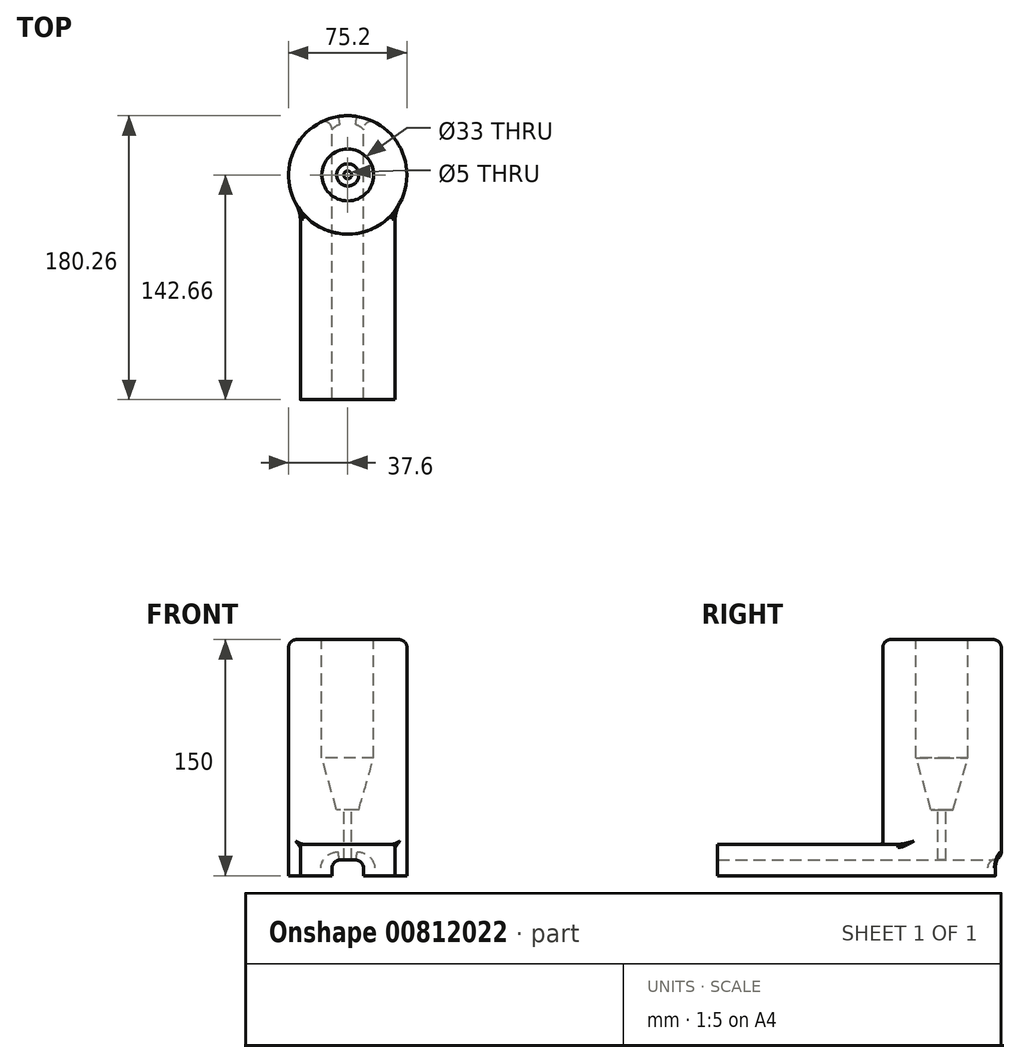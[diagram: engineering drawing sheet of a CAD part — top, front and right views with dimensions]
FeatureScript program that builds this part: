
annotation { "Feature Type Name" : "Feature", "Feature Type Description" : "" }
export const myFeature = defineFeature(function(context is Context, id is Id, definition is map)
    precondition{}
    {
        {
            var Q0;
            Q0=qCreatedBy(makeId("Front.planeOp"),FACE);
            var sketch = newSketch(context, id + "F0", { "sketchPlane" : qUnion([Q0])});
            skLineSegment(sketch, "E0.bottom", {"start": v(0, 0) * mm, "end": v(60, 0) * mm});
            skLineSegment(sketch, "E0.top", {"start": v(0, 20) * mm, "end": v(60, 20) * mm});
            skLineSegment(sketch, "E0.left", {"start": v(0, 0) * mm, "end": v(0, 20) * mm});
            skLineSegment(sketch, "E0.right", {"start": v(60, 0) * mm, "end": v(60, 20) * mm});
            skLineSegment(sketch, "E1.bottom", {"start": v(20, 0) * mm, "end": v(40, 0) * mm});
            skLineSegment(sketch, "E1.top", {"start": v(20, 10) * mm, "end": v(40, 10) * mm});
            skLineSegment(sketch, "E1.left", {"start": v(20, 0) * mm, "end": v(20, 10) * mm});
            skLineSegment(sketch, "E1.right", {"start": v(40, 0) * mm, "end": v(40, 10) * mm});
            skSolve(sketch);
        }
        {
            var Q0;
            Q0=makeQuery(id+"F0.imprint","IMPRINT",FACE,{"disambiguationData":[TD([[makeQuery(id+"F0.imprint","IMPRINT",EDGE,{"derivedFrom":sQuery(id+"F0.wireOp",EDGE,"E0.top")}),-1.0]])]});
            extrude(context, id + "F1", {"entities" : qUnion([Q0]), "depth" : 120 * mm, "offsetDistance" : 25 * mm});
        }
        {
            var Q0;
            Q0=qCreatedBy(makeId("Top.planeOp"),FACE);
            var sketch = newSketch(context, id + "F2", { "sketchPlane" : qUnion([Q0])});
            skPoint(sketch, "E2.0", {"position": v(60, 0) * mm});
            skCircle(sketch, "E3", {"center": v(30, 22.66) * mm, "radius": 37.6 * mm});
            skPoint(sketch, "E3.first.point", {"position": v(0, 0) * mm});
            skPoint(sketch, "E3.third.point", {"position": v(-4.6, 37.36) * mm});
            skSolve(sketch);
        }
        {
            var Q0;
            Q0=qSketchRegion(id+"F2",true);
            extrude(context, id + "F3", {"entities" : qUnion([Q0]), "operationType" : NewBodyOperationType.ADD, "depth" : 150 * mm, "offsetDistance" : 25 * mm});
        }
        {
            var Q0;
            Q0=makeQuery(id+"F0.imprint","IMPRINT",FACE,{"disambiguationData":[TD([[makeQuery(id+"F0.imprint","IMPRINT",EDGE,{"derivedFrom":sQuery(id+"F0.wireOp",EDGE,"E1.top")}),-1.0]])]});
            extrude(context, id + "F4", {"entities" : qUnion([Q0]), "operationType" : NewBodyOperationType.REMOVE, "endBound" : BoundingType.UP_TO_NEXT, "oppositeDirection" : true, "depth" : 25 * mm, "offsetDistance" : 25 * mm, "hasSecondDirection" : true, "secondDirectionOppositeDirection" : false, "secondDirectionDepth" : 25 * mm});
        }
        {
            var Q0;
            Q0=makeQuery(id+"F1.opExtrude","CAP_EDGE",EDGE,{"disambiguationData":[OSD([sQuery(id+"F0.wireOp",EDGE,"E0.right")])],"isStart":true});
            var Q1;
            Q1=makeQuery(id+"F1.opExtrude","CAP_EDGE",EDGE,{"disambiguationData":[OSD([sQuery(id+"F0.wireOp",EDGE,"E0.left")])],"isStart":true});
            fillet(context, id + "F5", {"entities" : qUnion([Q0, Q1]), "radius" : 25 * mm, "tangentPropagation" : true, "allowEdgeOverflow" : false});
        }
        {
            var Q0;
            Q0=makeQuery(id+"F3.opExtrude","CAP_FACE",FACE,{"disambiguationData":[OSD([sQuery(id+"F2.wireOp",EDGE,"E3")])],"isStart":false});
            var sketch = newSketch(context, id + "F6", { "sketchPlane" : qUnion([Q0])});
            skCircle(sketch, "E4.0", {"center": v(30, 22.66) * mm, "radius": 37.6 * mm});
            skCircle(sketch, "E5", {"center": v(30, 22.66) * mm, "radius": 16.5 * mm});
            skSolve(sketch);
        }
        {
            var Q0;
            Q0=makeQuery(id+"F6.imprint","IMPRINT",FACE,{"disambiguationData":[TD([[makeQuery(id+"F6.imprint","IMPRINT",EDGE,{"derivedFrom":sQuery(id+"F6.wireOp",EDGE,"E5")}),1.0]])]});
            extrude(context, id + "F7", {"entities" : qUnion([Q0]), "operationType" : NewBodyOperationType.REMOVE, "oppositeDirection" : true, "depth" : 75 * mm, "offsetDistance" : 25 * mm});
        }
        {
            var Q0;
            Q0=makeQuery(id+"F7.boolean.opBoolean","COPY",FACE,{"derivedFrom":makeQuery(id+"F7.opExtrude","CAP_FACE",FACE,{"disambiguationData":[OSD([sQuery(id+"F6.wireOp",EDGE,"E5")])],"isStart":false})});
            extrude(context, id + "F8", {"entities" : qUnion([Q0]), "operationType" : NewBodyOperationType.REMOVE, "oppositeDirection" : true, "depth" : 33 * mm, "offsetDistance" : 25 * mm, "hasDraft" : true, "draftAngle" : 16 * degree, "draftPullDirection" : true});
        }
        {
            var Q0;
            Q0=makeQuery(id+"F8.boolean.opBoolean","COPY",FACE,{"derivedFrom":makeQuery(id+"F8.opExtrude","CAP_FACE",FACE,{"disambiguationData":[OSD([sQuery(id+"F6.wireOp",EDGE,"E5")])],"isStart":false})});
            var sketch = newSketch(context, id + "F9", { "sketchPlane" : qUnion([Q0])});
            skCircle(sketch, "E6", {"center": v(30, 22.66) * mm, "radius": 2.5 * mm});
            skSolve(sketch);
        }
        {
            var Q0;
            Q0=qSketchRegion(id+"F9",true);
            extrude(context, id + "F10", {"entities" : qUnion([Q0]), "operationType" : NewBodyOperationType.REMOVE, "endBound" : BoundingType.UP_TO_NEXT, "oppositeDirection" : true, "depth" : 25 * mm, "offsetDistance" : 25 * mm});
        }
        {
            var Q0;
            Q0=makeQuery(id+"F3.boolean.opBoolean","INTERSECT",EDGE,{"derivedFrom":[makeQuery(id+"F1.opExtrude","SWEPT_FACE",FACE,{"disambiguationData":[OSD([sQuery(id+"F0.wireOp",EDGE,"E0.top")])]}),makeQuery(id+"F3.opExtrude","SWEPT_FACE",FACE,{"disambiguationData":[OSD([sQuery(id+"F2.wireOp",EDGE,"E3")])]})]});
            fillet(context, id + "F11", {"entities" : qUnion([Q0]), "radius" : 2 * mm, "tangentPropagation" : true, "allowEdgeOverflow" : false});
        }
        {
            var Q0;
            Q0=makeQuery(id+"F7.boolean.opBoolean","COPY",EDGE,{"derivedFrom":makeQuery(id+"F7.opExtrude","CAP_EDGE",EDGE,{"disambiguationData":[OSD([sQuery(id+"F6.wireOp",EDGE,"E5")])],"isStart":true})});
            var Q1;
            Q1=makeQuery(id+"F3.opExtrude","CAP_EDGE",EDGE,{"disambiguationData":[OSD([sQuery(id+"F2.wireOp",EDGE,"E3")])],"isStart":false});
            fillet(context, id + "F12", {"entities" : qUnion([Q0, Q1]), "radius" : 5 * mm, "tangentPropagation" : true, "allowEdgeOverflow" : false});
        }
        {
            var Q0;
            {var subQ0=sQuery(id+"F0.wireOp",EDGE,"E1.left");var subQ1=sQuery(id+"F0.wireOp",EDGE,"E1.top");Q0=makeQuery(id+"F4.boolean.opBoolean","MERGE",EDGE,{"derivedFrom":[makeQuery(id+"F1.opExtrude","SWEPT_EDGE",EDGE,{"disambiguationData":[OSD([subQ1,subQ0])]})],"fromTools":[makeQuery(id+"F4.opExtrude","SWEPT_EDGE",EDGE,{"disambiguationData":[OSD([subQ1,subQ0])]})]});}
            var Q1;
            {var subQ0=sQuery(id+"F0.wireOp",EDGE,"E1.right");var subQ1=sQuery(id+"F0.wireOp",EDGE,"E1.top");Q1=makeQuery(id+"F4.boolean.opBoolean","MERGE",EDGE,{"derivedFrom":[makeQuery(id+"F1.opExtrude","SWEPT_EDGE",EDGE,{"disambiguationData":[OSD([subQ1,subQ0])]})],"fromTools":[makeQuery(id+"F4.opExtrude","SWEPT_EDGE",EDGE,{"disambiguationData":[OSD([subQ1,subQ0])]})]});}
            fillet(context, id + "F13", {"entities" : qUnion([Q0, Q1]), "radius" : 5 * mm, "tangentPropagation" : true, "allowEdgeOverflow" : false});
        }
        {
            var Q0;
            Q0=makeQuery(id+"F1.opExtrude","SWEPT_EDGE",EDGE,{"disambiguationData":[OSD([sQuery(id+"F0.wireOp",EDGE,"E0.top"),sQuery(id+"F0.wireOp",EDGE,"E0.left")])]});
            var Q1;
            Q1=makeQuery(id+"F1.opExtrude","SWEPT_EDGE",EDGE,{"disambiguationData":[OSD([sQuery(id+"F0.wireOp",EDGE,"E0.top"),sQuery(id+"F0.wireOp",EDGE,"E0.right")])]});
            fillet(context, id + "F14", {"entities" : qUnion([Q0, Q1]), "radius" : 2 * mm, "tangentPropagation" : true, "allowEdgeOverflow" : false});
        }
        {
            var Q0;
            {var subQ3=sQuery(id+"F2.wireOp",EDGE,"E3");Q0=makeQuery(id+"F4.boolean.opBoolean","COPY",EDGE,{"derivedFrom":makeQuery(id+"F4.opExtrude","TWEAK_EDGE",EDGE,{"derivedFrom":[makeQuery(id+"F0.imprint","IMPRINT",EDGE,{"derivedFrom":sQuery(id+"F0.wireOp",EDGE,"E1.top")}),makeQuery(id+"F3.boolean.opBoolean","SPLIT",FACE,{"disambiguationData":[TD([makeQuery(id+"F1.opExtrude","SWEPT_FACE",FACE,{"disambiguationData":[OSD([sQuery(id+"F0.wireOp",EDGE,"E0.top")])]})])],"derivedFrom":makeQuery(id+"F3.opExtrude","SWEPT_FACE",FACE,{"disambiguationData":[OSD([subQ3])]})})]})});}
            var Q1;
            {var subQ2=sQuery(id+"F0.wireOp",EDGE,"E1.left");var subQ3=sQuery(id+"F2.wireOp",EDGE,"E3");var subQ5=sQuery(id+"F0.wireOp",EDGE,"E1.top");Q1=makeQuery(id+"F13.opFillet","BLEND_EDGE",EDGE,{"blendedFrom":[makeQuery(id+"F4.boolean.opBoolean","MERGE",EDGE,{"derivedFrom":[makeQuery(id+"F1.opExtrude","SWEPT_EDGE",EDGE,{"disambiguationData":[OSD([subQ5,subQ2])]})],"fromTools":[makeQuery(id+"F4.opExtrude","SWEPT_EDGE",EDGE,{"disambiguationData":[OSD([subQ5,subQ2])]})]}),makeQuery(id+"F3.boolean.opBoolean","SPLIT",FACE,{"disambiguationData":[TD([makeQuery(id+"F1.opExtrude","SWEPT_FACE",FACE,{"disambiguationData":[OSD([sQuery(id+"F0.wireOp",EDGE,"E0.top")])]})])],"derivedFrom":makeQuery(id+"F3.opExtrude","SWEPT_FACE",FACE,{"disambiguationData":[OSD([subQ3])]})})],"blendedInto":[makeQuery(id+"F3.boolean.opBoolean","SPLIT",FACE,{"disambiguationData":[TD([makeQuery(id+"F1.opExtrude","SWEPT_FACE",FACE,{"disambiguationData":[OSD([sQuery(id+"F0.wireOp",EDGE,"E0.top")])]})])],"derivedFrom":makeQuery(id+"F3.opExtrude","SWEPT_FACE",FACE,{"disambiguationData":[OSD([subQ3])]})})]});}
            var Q2;
            {var subQ2=sQuery(id+"F2.wireOp",EDGE,"E3");var subQ3=sQuery(id+"F0.wireOp",EDGE,"E1.right");var subQ5=sQuery(id+"F0.wireOp",EDGE,"E1.top");Q2=makeQuery(id+"F13.opFillet","BLEND_EDGE",EDGE,{"blendedFrom":[makeQuery(id+"F4.boolean.opBoolean","MERGE",EDGE,{"derivedFrom":[makeQuery(id+"F1.opExtrude","SWEPT_EDGE",EDGE,{"disambiguationData":[OSD([subQ5,subQ3])]})],"fromTools":[makeQuery(id+"F4.opExtrude","SWEPT_EDGE",EDGE,{"disambiguationData":[OSD([subQ5,subQ3])]})]}),makeQuery(id+"F3.boolean.opBoolean","SPLIT",FACE,{"disambiguationData":[TD([makeQuery(id+"F1.opExtrude","SWEPT_FACE",FACE,{"disambiguationData":[OSD([sQuery(id+"F0.wireOp",EDGE,"E0.top")])]})])],"derivedFrom":makeQuery(id+"F3.opExtrude","SWEPT_FACE",FACE,{"disambiguationData":[OSD([subQ2])]})})],"blendedInto":[makeQuery(id+"F3.boolean.opBoolean","SPLIT",FACE,{"disambiguationData":[TD([makeQuery(id+"F1.opExtrude","SWEPT_FACE",FACE,{"disambiguationData":[OSD([sQuery(id+"F0.wireOp",EDGE,"E0.top")])]})])],"derivedFrom":makeQuery(id+"F3.opExtrude","SWEPT_FACE",FACE,{"disambiguationData":[OSD([subQ2])]})})]});}
            var Q3;
            {var subQ2=sQuery(id+"F0.wireOp",EDGE,"E1.right");var subQ4=sQuery(id+"F2.wireOp",EDGE,"E3");Q3=makeQuery(id+"F4.boolean.opBoolean","COPY",EDGE,{"derivedFrom":makeQuery(id+"F4.opExtrude","TWEAK_EDGE",EDGE,{"derivedFrom":[makeQuery(id+"F0.imprint","IMPRINT",EDGE,{"derivedFrom":subQ2}),makeQuery(id+"F3.boolean.opBoolean","SPLIT",FACE,{"disambiguationData":[TD([makeQuery(id+"F1.opExtrude","SWEPT_FACE",FACE,{"disambiguationData":[OSD([sQuery(id+"F0.wireOp",EDGE,"E0.top")])]})])],"derivedFrom":makeQuery(id+"F3.opExtrude","SWEPT_FACE",FACE,{"disambiguationData":[OSD([subQ4])]})})]})});}
            var Q4;
            {var subQ3=sQuery(id+"F2.wireOp",EDGE,"E3");var subQ5=sQuery(id+"F0.wireOp",EDGE,"E1.left");Q4=makeQuery(id+"F4.boolean.opBoolean","COPY",EDGE,{"derivedFrom":makeQuery(id+"F4.opExtrude","TWEAK_EDGE",EDGE,{"derivedFrom":[makeQuery(id+"F0.imprint","IMPRINT",EDGE,{"derivedFrom":subQ5}),makeQuery(id+"F3.boolean.opBoolean","SPLIT",FACE,{"disambiguationData":[TD([makeQuery(id+"F1.opExtrude","SWEPT_FACE",FACE,{"disambiguationData":[OSD([sQuery(id+"F0.wireOp",EDGE,"E0.top")])]})])],"derivedFrom":makeQuery(id+"F3.opExtrude","SWEPT_FACE",FACE,{"disambiguationData":[OSD([subQ3])]})})]})});}
            fillet(context, id + "F15", {"entities" : qUnion([Q0, Q1, Q2, Q3, Q4]), "radius" : 5 * mm, "tangentPropagation" : true, "allowEdgeOverflow" : false});
        }
    });
